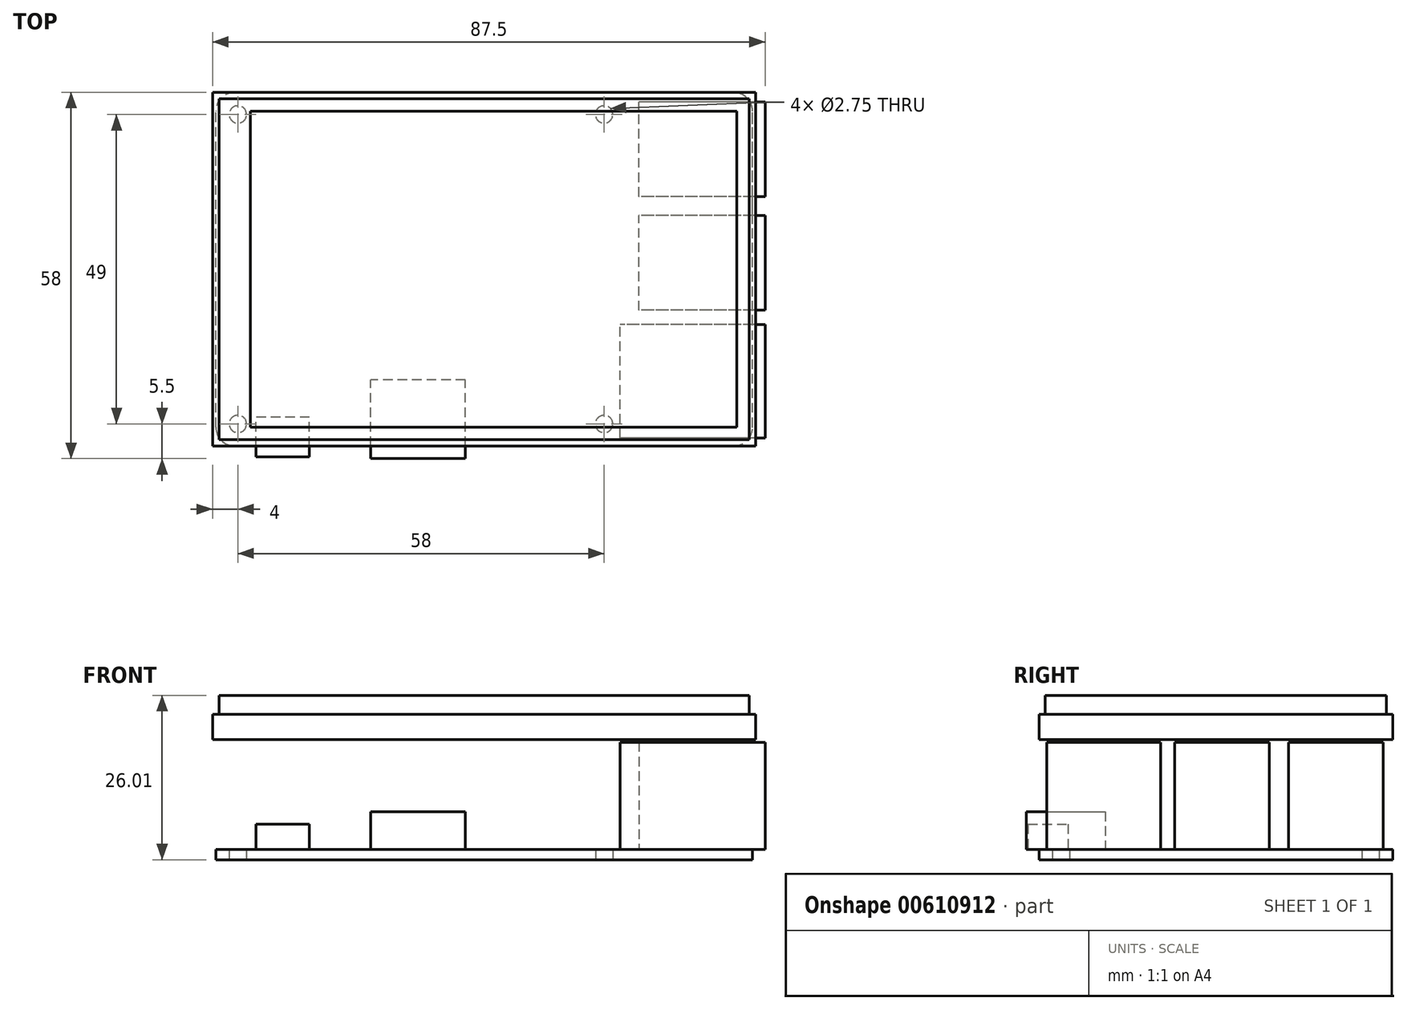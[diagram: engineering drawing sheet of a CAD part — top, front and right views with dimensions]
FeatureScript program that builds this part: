
annotation { "Feature Type Name" : "Feature", "Feature Type Description" : "" }
export const myFeature = defineFeature(function(context is Context, id is Id, definition is map)
    precondition{}
    {
        {
            var Q0;
            Q0=qCreatedBy(makeId("Top.planeOp"),FACE);
            var sketch = newSketch(context, id + "F0", { "sketchPlane" : qUnion([Q0])});
            skLineSegment(sketch, "E0.bottom", {"start": v(39.5, -28) * mm, "end": v(-39.5, -28) * mm});
            skLineSegment(sketch, "E0.top", {"start": v(39.5, 28) * mm, "end": v(-39.5, 28) * mm});
            skLineSegment(sketch, "E0.left", {"start": v(42.5, -25) * mm, "end": v(42.5, 25) * mm});
            skLineSegment(sketch, "E0.right", {"start": v(-42.5, -25) * mm, "end": v(-42.5, 25) * mm});
            skPoint(sketch, "E0.middle", {"position": v(0, 0) * mm});
            skPoint(sketch, "E1.visualSharp", {"position": v(-42.5, 28) * mm});
            skArc(sketch, "E1.filletArc", {"start": v(-39.5, 28) * mm, "mid": v(-41.62, 27.12) * mm, "end": v(-42.5, 25) * mm});
            skPoint(sketch, "E2.visualSharp", {"position": v(42.5, 28) * mm});
            skArc(sketch, "E2.filletArc", {"start": v(42.5, 25) * mm, "mid": v(41.62, 27.12) * mm, "end": v(39.5, 28) * mm});
            skPoint(sketch, "E3.visualSharp", {"position": v(-42.5, -28) * mm});
            skArc(sketch, "E3.filletArc", {"start": v(-42.5, -25) * mm, "mid": v(-41.62, -27.12) * mm, "end": v(-39.5, -28) * mm});
            skPoint(sketch, "E4.visualSharp", {"position": v(42.5, -28) * mm});
            skArc(sketch, "E4.filletArc", {"start": v(39.5, -28) * mm, "mid": v(41.62, -27.12) * mm, "end": v(42.5, -25) * mm});
            skCircle(sketch, "E5", {"center": v(-39, 24.5) * mm, "radius": 1.38 * mm});
            skCircle(sketch, "E6", {"center": v(19, 24.5) * mm, "radius": 1.38 * mm});
            skCircle(sketch, "E7", {"center": v(-39, -24.5) * mm, "radius": 1.38 * mm});
            skCircle(sketch, "E8", {"center": v(19, -24.5) * mm, "radius": 1.38 * mm});
            skSolve(sketch);
        }
        {
            var Q0;
            Q0=makeQuery(id+"F0.imprint","IMPRINT",FACE,{"disambiguationData":[TD([[makeQuery(id+"F0.imprint","IMPRINT",EDGE,{"derivedFrom":sQuery(id+"F0.wireOp",EDGE,"E0.bottom")}),-1.0]])]});
            extrude(context, id + "F1", {"entities" : qUnion([Q0]), "depth" : 1.6 * mm});
        }
        {
            var Q0;
            Q0=makeQuery(id+"F1.opExtrude","CAP_FACE",FACE,{"disambiguationData":[OSD([sQuery(id+"F0.wireOp",EDGE,"E0.bottom"),sQuery(id+"F0.wireOp",EDGE,"E0.top"),sQuery(id+"F0.wireOp",EDGE,"E0.left"),sQuery(id+"F0.wireOp",EDGE,"E0.right"),sQuery(id+"F0.wireOp",EDGE,"E1.filletArc"),sQuery(id+"F0.wireOp",EDGE,"E2.filletArc"),sQuery(id+"F0.wireOp",EDGE,"E3.filletArc"),sQuery(id+"F0.wireOp",EDGE,"E4.filletArc"),sQuery(id+"F0.wireOp",EDGE,"E5"),sQuery(id+"F0.wireOp",EDGE,"E6"),sQuery(id+"F0.wireOp",EDGE,"E7"),sQuery(id+"F0.wireOp",EDGE,"E8")])],"isStart":false});
            var sketch = newSketch(context, id + "F2", { "sketchPlane" : qUnion([Q0])});
            skLineSegment(sketch, "E9.bottom", {"start": v(-27.67, -29.74) * mm, "end": v(-36.13, -29.74) * mm});
            skLineSegment(sketch, "E9.top", {"start": v(-27.67, -23.43) * mm, "end": v(-36.13, -23.43) * mm});
            skLineSegment(sketch, "E9.left", {"start": v(-27.67, -29.74) * mm, "end": v(-27.67, -23.43) * mm});
            skLineSegment(sketch, "E9.right", {"start": v(-36.13, -29.74) * mm, "end": v(-36.13, -23.43) * mm});
            skPoint(sketch, "E9.middle", {"position": v(-31.9, -26.59) * mm});
            skSolve(sketch);
        }
        {
            var Q0;
            {var subQ0=sQuery(id+"F2.wireOp",EDGE,"E9.bottom");Q0=makeQuery(id+"F2.imprint","IMPRINT",FACE,{"disambiguationData":[TD([[makeQuery(id+"F2.imprint","IMPRINT",EDGE,{"derivedFrom":subQ0}),-1.0]])]});}
            var Q1;
            {var subQ0=sQuery(id+"F2.wireOp",EDGE,"E9.top");Q1=makeQuery(id+"F2.imprint","IMPRINT",FACE,{"disambiguationData":[TD([[makeQuery(id+"F2.imprint","IMPRINT",EDGE,{"derivedFrom":subQ0}),1.0]])]});}
            extrude(context, id + "F3", {"entities" : qUnion([Q0, Q1]), "operationType" : NewBodyOperationType.ADD, "depth" : 4 * mm});
        }
        {
            var Q0;
            Q0=makeQuery(id+"F1.opExtrude","CAP_FACE",FACE,{"disambiguationData":[OSD([sQuery(id+"F0.wireOp",EDGE,"E0.bottom"),sQuery(id+"F0.wireOp",EDGE,"E0.top"),sQuery(id+"F0.wireOp",EDGE,"E0.left"),sQuery(id+"F0.wireOp",EDGE,"E0.right"),sQuery(id+"F0.wireOp",EDGE,"E1.filletArc"),sQuery(id+"F0.wireOp",EDGE,"E2.filletArc"),sQuery(id+"F0.wireOp",EDGE,"E3.filletArc"),sQuery(id+"F0.wireOp",EDGE,"E4.filletArc"),sQuery(id+"F0.wireOp",EDGE,"E5"),sQuery(id+"F0.wireOp",EDGE,"E6"),sQuery(id+"F0.wireOp",EDGE,"E7"),sQuery(id+"F0.wireOp",EDGE,"E8")])],"isStart":false});
            var sketch = newSketch(context, id + "F4", { "sketchPlane" : qUnion([Q0])});
            skLineSegment(sketch, "E10.bottom", {"start": v(44.5, 11.5) * mm, "end": v(24.5, 11.5) * mm});
            skLineSegment(sketch, "E10.top", {"start": v(44.5, 26.5) * mm, "end": v(24.5, 26.5) * mm});
            skLineSegment(sketch, "E10.left", {"start": v(44.5, 11.5) * mm, "end": v(44.5, 26.5) * mm});
            skLineSegment(sketch, "E10.right", {"start": v(24.5, 11.5) * mm, "end": v(24.5, 26.5) * mm});
            skPoint(sketch, "E10.middle", {"position": v(34.5, 19) * mm});
            skLineSegment(sketch, "E11.bottom", {"start": v(44.5, -6.5) * mm, "end": v(24.5, -6.5) * mm});
            skLineSegment(sketch, "E11.top", {"start": v(44.5, 8.5) * mm, "end": v(24.5, 8.5) * mm});
            skLineSegment(sketch, "E11.left", {"start": v(44.5, -6.5) * mm, "end": v(44.5, 8.5) * mm});
            skLineSegment(sketch, "E11.right", {"start": v(24.5, -6.5) * mm, "end": v(24.5, 8.5) * mm});
            skPoint(sketch, "E11.middle", {"position": v(34.5, 1) * mm});
            skLineSegment(sketch, "E12.bottom", {"start": v(44.5, -26.75) * mm, "end": v(21.5, -26.75) * mm});
            skLineSegment(sketch, "E12.top", {"start": v(44.5, -8.75) * mm, "end": v(21.5, -8.75) * mm});
            skLineSegment(sketch, "E12.left", {"start": v(44.5, -26.75) * mm, "end": v(44.5, -8.75) * mm});
            skLineSegment(sketch, "E12.right", {"start": v(21.5, -26.75) * mm, "end": v(21.5, -8.75) * mm});
            skPoint(sketch, "E12.middle", {"position": v(33, -17.75) * mm});
            skSolve(sketch);
        }
        {
            var Q0;
            Q0=qSketchRegion(id+"F4",true);
            extrude(context, id + "F5", {"entities" : qUnion([Q0]), "operationType" : NewBodyOperationType.ADD, "depth" : 17 * mm});
        }
        {
            var Q0;
            Q0=makeQuery(id+"F1.opExtrude","CAP_FACE",FACE,{"disambiguationData":[OSD([sQuery(id+"F0.wireOp",EDGE,"E0.bottom"),sQuery(id+"F0.wireOp",EDGE,"E0.top"),sQuery(id+"F0.wireOp",EDGE,"E0.left"),sQuery(id+"F0.wireOp",EDGE,"E0.right"),sQuery(id+"F0.wireOp",EDGE,"E1.filletArc"),sQuery(id+"F0.wireOp",EDGE,"E2.filletArc"),sQuery(id+"F0.wireOp",EDGE,"E3.filletArc"),sQuery(id+"F0.wireOp",EDGE,"E4.filletArc"),sQuery(id+"F0.wireOp",EDGE,"E5"),sQuery(id+"F0.wireOp",EDGE,"E6"),sQuery(id+"F0.wireOp",EDGE,"E7"),sQuery(id+"F0.wireOp",EDGE,"E8")])],"isStart":false});
            var sketch = newSketch(context, id + "F6", { "sketchPlane" : qUnion([Q0])});
            skLineSegment(sketch, "E13.bottom", {"start": v(-3, -30) * mm, "end": v(-18, -30) * mm});
            skLineSegment(sketch, "E13.top", {"start": v(-3, -17.5) * mm, "end": v(-18, -17.5) * mm});
            skLineSegment(sketch, "E13.left", {"start": v(-3, -30) * mm, "end": v(-3, -17.5) * mm});
            skLineSegment(sketch, "E13.right", {"start": v(-18, -30) * mm, "end": v(-18, -17.5) * mm});
            skPoint(sketch, "E13.middle", {"position": v(-10.5, -23.75) * mm});
            skSolve(sketch);
        }
        {
            var Q0;
            Q0=qSketchRegion(id+"F6",true);
            extrude(context, id + "F7", {"entities" : qUnion([Q0]), "operationType" : NewBodyOperationType.ADD, "depth" : 6 * mm});
        }
        {
            var Q0;
            Q0=qCreatedBy(makeId("Top.planeOp"),FACE);
            cPlane(context, id + "F8", {"entities" : qUnion([Q0]), "cplaneType" : CPlaneType.OFFSET, "offset" : 23 * mm, "width" : 150 * mm, "height" : 150 * mm});
        }
        {
            var Q0;
            Q0=qCreatedBy(id+"F8.planeOp",FACE);
            var sketch = newSketch(context, id + "F9", { "sketchPlane" : qUnion([Q0])});
            skLineSegment(sketch, "E14.bottom", {"start": v(42, -27) * mm, "end": v(-42, -27) * mm});
            skLineSegment(sketch, "E14.top", {"start": v(42, 27) * mm, "end": v(-42, 27) * mm});
            skLineSegment(sketch, "E14.left", {"start": v(42, -27) * mm, "end": v(42, 27) * mm});
            skLineSegment(sketch, "E14.right", {"start": v(-42, -27) * mm, "end": v(-42, 27) * mm});
            skPoint(sketch, "E14.middle", {"position": v(0, 0) * mm});
            skSolve(sketch);
        }
        {
            var Q0;
            Q0 = qSketchRegion(id + "F9", true);
            extrude(context, id + "F10", {"entities" : qUnion([Q0]), "depth" : 3 * mm, "offsetDistance" : 25 * mm});
        }
        {
            var Q0;
            Q0=makeQuery(id+"F10.opExtrude","CAP_FACE",FACE,{"disambiguationData":[OSD([sQuery(id+"F9.wireOp",EDGE,"E14.bottom"),sQuery(id+"F9.wireOp",EDGE,"E14.top"),sQuery(id+"F9.wireOp",EDGE,"E14.left"),sQuery(id+"F9.wireOp",EDGE,"E14.right")])],"isStart":false});
            var sketch = newSketch(context, id + "F11", { "sketchPlane" : qUnion([Q0])});
            skLineSegment(sketch, "E15.bottom", {"start": v(-37, 25) * mm, "end": v(40, 25) * mm});
            skLineSegment(sketch, "E15.top", {"start": v(-37, -25) * mm, "end": v(40, -25) * mm});
            skLineSegment(sketch, "E15.left", {"start": v(-37, 25) * mm, "end": v(-37, -25) * mm});
            skLineSegment(sketch, "E15.right", {"start": v(40, 25) * mm, "end": v(40, -25) * mm});
            skSolve(sketch);
        }
        {
            var Q0;
            Q0 = qSketchRegion(id + "F11", true);
            extrude(context, id + "F12", {"entities" : qUnion([Q0]), "operationType" : NewBodyOperationType.ADD, "depth" : 0.01 * mm, "offsetDistance" : 25 * mm});
        }
        {
            var Q0;
            Q0=makeQuery(id+"F10.opExtrude","CAP_FACE",FACE,{"disambiguationData":[OSD([sQuery(id+"F9.wireOp",EDGE,"E14.bottom"),sQuery(id+"F9.wireOp",EDGE,"E14.top"),sQuery(id+"F9.wireOp",EDGE,"E14.left"),sQuery(id+"F9.wireOp",EDGE,"E14.right")])],"isStart":true});
            var sketch = newSketch(context, id + "F13", { "sketchPlane" : qUnion([Q0])});
            skPoint(sketch, "E16.middle", {"position": v(0, 0) * mm});
            skLineSegment(sketch, "E17.bottom", {"start": v(43, -28) * mm, "end": v(-43, -28) * mm});
            skLineSegment(sketch, "E17.top", {"start": v(43, 28) * mm, "end": v(-43, 28) * mm});
            skLineSegment(sketch, "E17.left", {"start": v(43, -28) * mm, "end": v(43, 28) * mm});
            skLineSegment(sketch, "E17.right", {"start": v(-43, -28) * mm, "end": v(-43, 28) * mm});
            skSolve(sketch);
        }
        {
            var Q0;
            Q0 = qSketchRegion(id + "F13", true);
            extrude(context, id + "F14", {"entities" : qUnion([Q0]), "operationType" : NewBodyOperationType.ADD, "depth" : 4 * mm, "offsetDistance" : 25 * mm});
        }
    });
